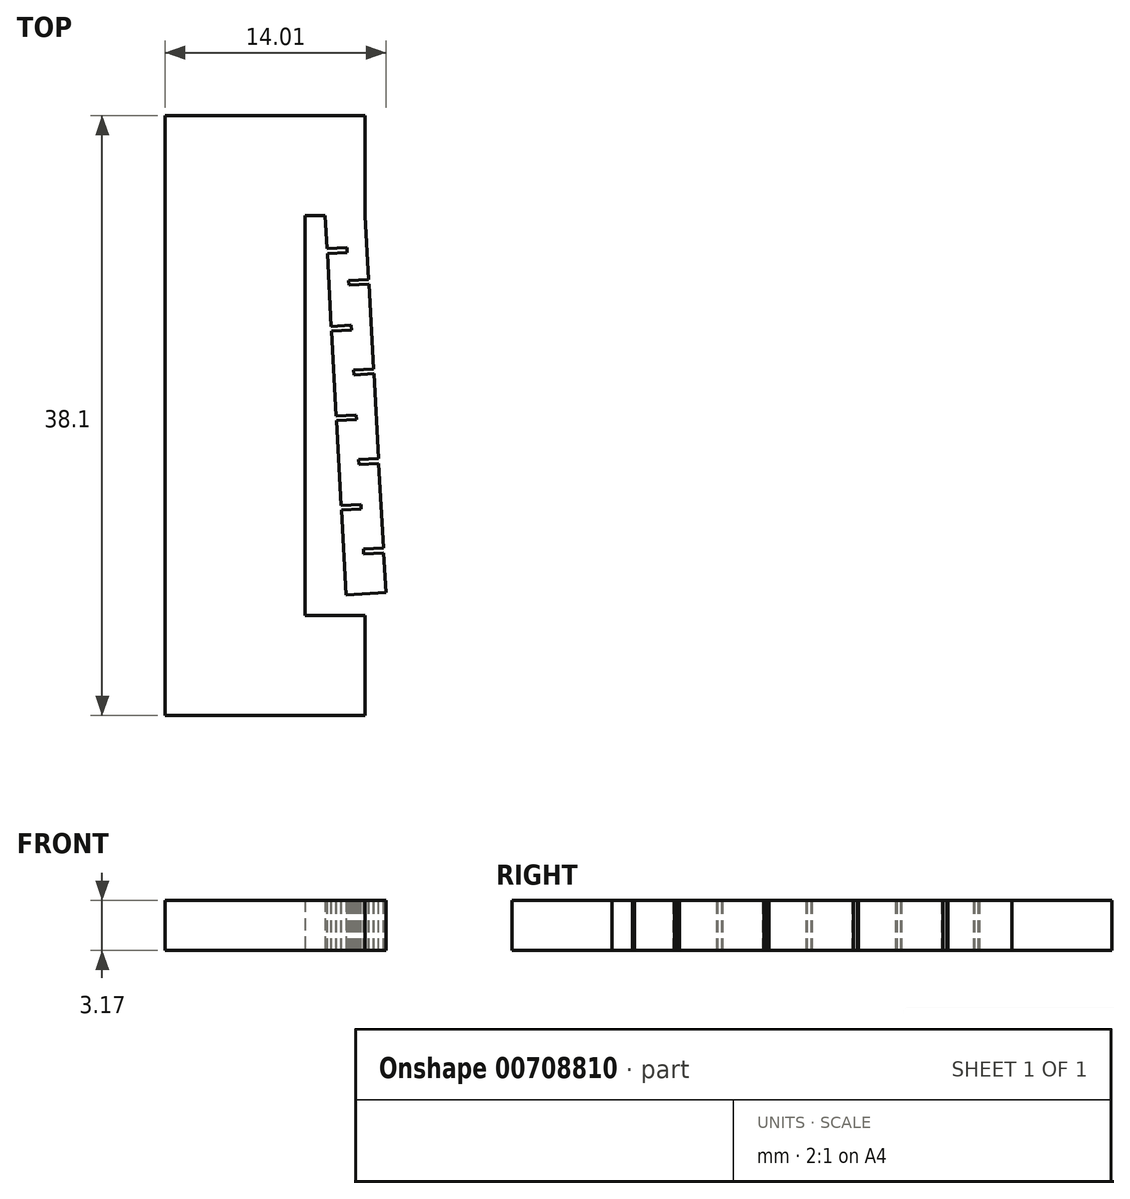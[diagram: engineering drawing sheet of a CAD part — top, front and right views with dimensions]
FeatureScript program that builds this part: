
annotation { "Feature Type Name" : "Feature", "Feature Type Description" : "" }
export const myFeature = defineFeature(function(context is Context, id is Id, definition is map)
    precondition{}
    {
        {
            var Q0;
            Q0=qCreatedBy(makeId("Top.planeOp"),FACE);
            var sketch = newSketch(context, id + "F0", { "sketchPlane" : qUnion([Q0])});
            skLineSegment(sketch, "E0.bottom", {"start": v(0, 0) * mm, "end": v(12.7, 0) * mm});
            skLineSegment(sketch, "E0.top", {"start": v(0, 38.1) * mm, "end": v(12.7, 38.1) * mm});
            skLineSegment(sketch, "E0.left", {"start": v(0, 0) * mm, "end": v(0, 38.1) * mm});
            skLineSegment(sketch, "E0.right", {"start": v(12.7, 0) * mm, "end": v(12.7, 6.35) * mm});
            skLineSegment(sketch, "E1.top", {"start": v(12.7, 6.35) * mm, "end": v(10.16, 6.35) * mm});
            skLineSegment(sketch, "E1.right", {"start": v(10.16, 31.75) * mm, "end": v(10.16, 6.35) * mm});
            skLineSegment(sketch, "E2.trimOffspring", {"start": v(12.7, 31.75) * mm, "end": v(12.7, 38.1) * mm});
            skLineSegment(sketch, "E3", {"start": v(10.16, 31.75) * mm, "end": v(11.47, 7.66) * mm});
            skLineSegment(sketch, "E4", {"start": v(11.47, 7.66) * mm, "end": v(14, 7.8) * mm});
            skLineSegment(sketch, "E5", {"start": v(14, 7.8) * mm, "end": v(12.7, 31.75) * mm});
            skLineSegment(sketch, "E6.bottom", {"start": v(10.16, 31.75) * mm, "end": v(8.9, 31.75) * mm});
            skLineSegment(sketch, "E6.top", {"start": v(10.16, 6.35) * mm, "end": v(8.9, 6.35) * mm});
            skLineSegment(sketch, "E6.right", {"start": v(8.9, 31.75) * mm, "end": v(8.9, 6.35) * mm});
            skSolve(sketch);
        }
        {
            var Q0;
            {var subQ1=sQuery(id+"F0.wireOp",EDGE,"E0.bottom");Q0=makeQuery(id+"F0.imprint","IMPRINT",FACE,{"disambiguationData":[TD([[makeQuery(id+"F0.imprint","IMPRINT",EDGE,{"derivedFrom":subQ1}),1.0]])]});}
            extrude(context, id + "F1", {"entities" : qUnion([Q0]), "depth" : 3.17 * mm, "offsetDistance" : 25.4 * mm});
        }
        {
            var Q0;
            Q0=makeQuery(id+"F1.opExtrude","CAP_FACE",FACE,{"disambiguationData":[OSD([sQuery(id+"F0.wireOp",EDGE,"E0.bottom"),sQuery(id+"F0.wireOp",EDGE,"E0.top"),sQuery(id+"F0.wireOp",EDGE,"E0.left"),sQuery(id+"F0.wireOp",EDGE,"E0.right"),sQuery(id+"F0.wireOp",EDGE,"E1.top"),sQuery(id+"F0.wireOp",EDGE,"E1.right"),sQuery(id+"F0.wireOp",EDGE,"E2.trimOffspring"),sQuery(id+"F0.wireOp",EDGE,"E3"),sQuery(id+"F0.wireOp",EDGE,"E4"),sQuery(id+"F0.wireOp",EDGE,"E5")])],"isStart":false});
            var sketch = newSketch(context, id + "F2", { "sketchPlane" : qUnion([Q0])});
            skLineSegment(sketch, "E7", {"start": v(13.87, 10.33) * mm, "end": v(12.6, 10.26) * mm});
            skLineSegment(sketch, "E8", {"start": v(12.6, 10.26) * mm, "end": v(12.59, 10.57) * mm});
            skLineSegment(sketch, "E9", {"start": v(12.59, 10.57) * mm, "end": v(13.85, 10.63) * mm});
            skLineSegment(sketch, "E10", {"start": v(13.85, 10.63) * mm, "end": v(13.87, 10.33) * mm});
            skLineSegment(sketch, "E11", {"start": v(11.18, 13.03) * mm, "end": v(12.45, 13.1) * mm});
            skLineSegment(sketch, "E12", {"start": v(12.45, 13.1) * mm, "end": v(12.43, 13.4) * mm});
            skLineSegment(sketch, "E13", {"start": v(12.43, 13.4) * mm, "end": v(11.16, 13.34) * mm});
            skLineSegment(sketch, "E14", {"start": v(11.16, 13.34) * mm, "end": v(11.18, 13.03) * mm});
            skLineSegment(sketch, "E15", {"start": v(13.54, 16.32) * mm, "end": v(12.27, 16.25) * mm});
            skLineSegment(sketch, "E16", {"start": v(12.27, 16.25) * mm, "end": v(12.3, 15.95) * mm});
            skLineSegment(sketch, "E17", {"start": v(12.3, 15.95) * mm, "end": v(13.56, 16.02) * mm});
            skLineSegment(sketch, "E18", {"start": v(13.56, 16.02) * mm, "end": v(13.54, 16.32) * mm});
            skLineSegment(sketch, "E19", {"start": v(10.85, 19.02) * mm, "end": v(12.12, 19.1) * mm});
            skLineSegment(sketch, "E20", {"start": v(12.12, 19.1) * mm, "end": v(12.14, 18.79) * mm});
            skLineSegment(sketch, "E21", {"start": v(12.14, 18.79) * mm, "end": v(10.87, 18.72) * mm});
            skLineSegment(sketch, "E22", {"start": v(10.87, 18.72) * mm, "end": v(10.85, 19.02) * mm});
            skLineSegment(sketch, "E23", {"start": v(13.23, 22) * mm, "end": v(11.96, 21.94) * mm});
            skLineSegment(sketch, "E24", {"start": v(11.96, 21.94) * mm, "end": v(11.98, 21.63) * mm});
            skLineSegment(sketch, "E25", {"start": v(11.98, 21.63) * mm, "end": v(13.25, 21.7) * mm});
            skLineSegment(sketch, "E26", {"start": v(13.25, 21.7) * mm, "end": v(13.23, 22) * mm});
            skLineSegment(sketch, "E27", {"start": v(10.54, 24.71) * mm, "end": v(11.81, 24.78) * mm});
            skLineSegment(sketch, "E28", {"start": v(11.81, 24.78) * mm, "end": v(11.83, 24.48) * mm});
            skLineSegment(sketch, "E29", {"start": v(11.83, 24.48) * mm, "end": v(10.56, 24.4) * mm});
            skLineSegment(sketch, "E30", {"start": v(10.56, 24.4) * mm, "end": v(10.54, 24.71) * mm});
            skLineSegment(sketch, "E31", {"start": v(12.94, 27.39) * mm, "end": v(11.67, 27.32) * mm});
            skLineSegment(sketch, "E32", {"start": v(11.67, 27.32) * mm, "end": v(11.65, 27.62) * mm});
            skLineSegment(sketch, "E33", {"start": v(11.65, 27.62) * mm, "end": v(12.92, 27.7) * mm});
            skLineSegment(sketch, "E34", {"start": v(12.92, 27.7) * mm, "end": v(12.94, 27.39) * mm});
            skLineSegment(sketch, "E35", {"start": v(10.3, 29.35) * mm, "end": v(11.56, 29.41) * mm});
            skLineSegment(sketch, "E36", {"start": v(11.56, 29.41) * mm, "end": v(11.54, 29.72) * mm});
            skLineSegment(sketch, "E37", {"start": v(11.54, 29.72) * mm, "end": v(10.27, 29.65) * mm});
            skLineSegment(sketch, "E38", {"start": v(10.27, 29.65) * mm, "end": v(10.3, 29.35) * mm});
            skLineSegment(sketch, "E39", {"start": v(11.47, 7.66) * mm, "end": v(12.72, 7.72) * mm});
            skLineSegment(sketch, "E40", {"start": v(12.72, 7.72) * mm, "end": v(12.74, 7.42) * mm});
            skLineSegment(sketch, "E41", {"start": v(12.74, 7.42) * mm, "end": v(11.47, 7.35) * mm});
            skLineSegment(sketch, "E42", {"start": v(11.47, 7.35) * mm, "end": v(11.47, 7.66) * mm});
            skLineSegment(sketch, "E43", {"start": v(14.07, 6.74) * mm, "end": v(12.8, 6.67) * mm});
            skLineSegment(sketch, "E44", {"start": v(12.8, 6.67) * mm, "end": v(12.81, 6.37) * mm});
            skLineSegment(sketch, "E45", {"start": v(12.81, 6.37) * mm, "end": v(14.08, 6.44) * mm});
            skLineSegment(sketch, "E46", {"start": v(14.08, 6.44) * mm, "end": v(14.07, 6.74) * mm});
            skSolve(sketch);
        }
        {
            var Q0;
            Q0=qSketchRegion(id+"F2",true);
            extrude(context, id + "F3", {"entities" : qUnion([Q0]), "operationType" : NewBodyOperationType.REMOVE, "endBound" : BoundingType.THROUGH_ALL, "oppositeDirection" : true, "depth" : 25.4 * mm, "offsetDistance" : 25.4 * mm});
        }
    });
